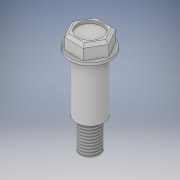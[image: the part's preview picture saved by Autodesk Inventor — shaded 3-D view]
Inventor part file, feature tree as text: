
AUTODESK INVENTOR PART (.ipt)
format: ipt  version: 2019 (Build 230136000, 136)  size: 142,848 bytes
history: native  units: mm
features: extrude x5, sketch x5, other x1, thread x1, chamfer x1
ambient origin geometry x8: Origin, YZ Plane, XZ Plane, XY Plane, X Axis, Y Axis, Z Axis, Center Point
bodies: Body1 (feature_tree)
feature tree (13):
  other  "Sólido1"
  extrude  "Extrusión1"  Depth=1.0mm TaperAngle=0.0deg
  extrude  "Extrusión2"  TaperAngle=0.0deg  [1 undecoded]
  extrude  "Extrusión3"  Depth=10.0mm
  extrude  "Extrusión4"  Depth=7.0mm
  thread  "Rosca2"  [1 undecoded]
  chamfer  "Chaflán1"  Distance=10.0mm
  extrude  "Extrusión5"  Depth=1.0mm
  sketch  "Boceto1"  dims[d0=15.0mm d1=1.0mm d2=0.0mm]
  sketch  "Boceto2"  dims[d3=6.0mm d4=0.0mm]
  sketch  "Boceto3"  dims[d5=5.0mm d6=0.0mm d7=10.0mm]
  sketch  "Boceto5"  dims[d8=21.0mm d9=0.0mm d15=7.0mm d16=11.0mm d17=0.0mm d18=10.0mm d19=0.0mm]
  sketch  "Boceto6"  dims[d20=1.0mm d21=2.0mm d22=45.0deg d23=9.0mm d24=1.0mm d25=0.0mm]
note: 2 required parameter values undecoded (feature->parameter linkage not recoverable at this tier; creation-order binding heuristic only, values carry confidence <= 0.55)
